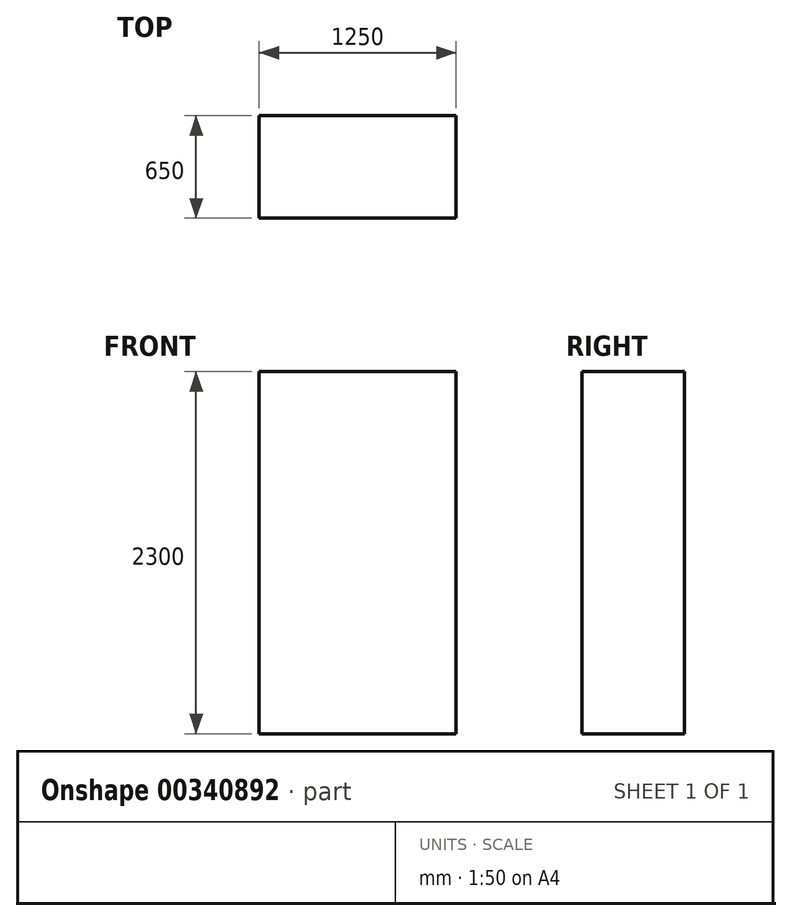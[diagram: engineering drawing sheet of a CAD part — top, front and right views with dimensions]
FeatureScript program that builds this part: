
annotation { "Feature Type Name" : "Feature", "Feature Type Description" : "" }
export const myFeature = defineFeature(function(context is Context, id is Id, definition is map)
    precondition{}
    {
        {
            var Q0;
            Q0=qCreatedBy(makeId("Top.planeOp"),FACE);
            var sketch = newSketch(context, id + "F0", { "sketchPlane" : qUnion([Q0])});
            skLineSegment(sketch, "E0.bottom", {"start": v(-58.82, 607.43) * mm, "end": v(1191.18, 607.43) * mm});
            skLineSegment(sketch, "E0.top", {"start": v(-58.82, -42.57) * mm, "end": v(1191.18, -42.57) * mm});
            skLineSegment(sketch, "E0.left", {"start": v(-58.82, 607.43) * mm, "end": v(-58.82, -42.57) * mm});
            skLineSegment(sketch, "E0.right", {"start": v(1191.18, 607.43) * mm, "end": v(1191.18, -42.57) * mm});
            skSolve(sketch);
        }
        {
            var Q0;
            Q0=qSketchRegion(id+"F0",true);
            extrude(context, id + "F1", {"entities" : qUnion([Q0]), "depth" : 2300 * mm});
        }
    });
